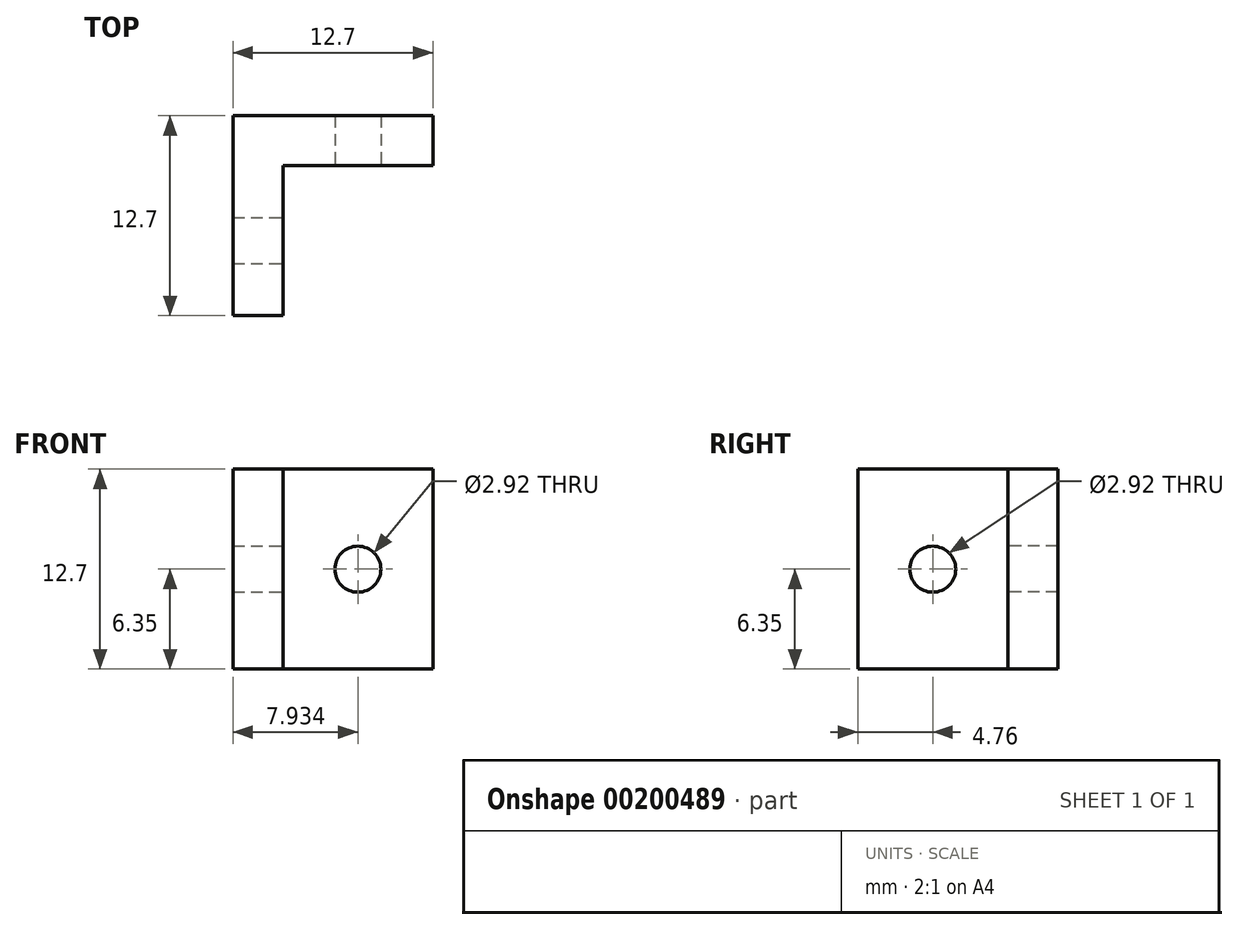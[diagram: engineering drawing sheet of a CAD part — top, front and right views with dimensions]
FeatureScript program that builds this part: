
annotation { "Feature Type Name" : "Feature", "Feature Type Description" : "" }
export const myFeature = defineFeature(function(context is Context, id is Id, definition is map)
    precondition{}
    {
        {
            var Q0;
            Q0=qCreatedBy(makeId("Top.planeOp"),FACE);
            var sketch = newSketch(context, id + "F0", { "sketchPlane" : qUnion([Q0])});
            skLineSegment(sketch, "E0", {"start": v(-46.71, 19.35) * mm, "end": v(-46.71, 32.05) * mm});
            skLineSegment(sketch, "E1", {"start": v(-46.71, 32.05) * mm, "end": v(-34.01, 32.05) * mm});
            skLineSegment(sketch, "E2", {"start": v(-46.71, 19.35) * mm, "end": v(-43.54, 19.35) * mm});
            skLineSegment(sketch, "E3", {"start": v(-43.54, 19.35) * mm, "end": v(-43.54, 32.05) * mm});
            skLineSegment(sketch, "E4", {"start": v(-43.54, 32.05) * mm, "end": v(-43.54, 28.87) * mm});
            skLineSegment(sketch, "E5", {"start": v(-43.54, 28.87) * mm, "end": v(-34.01, 28.87) * mm});
            skLineSegment(sketch, "E6", {"start": v(-34.01, 28.87) * mm, "end": v(-34.01, 32.05) * mm});
            skSolve(sketch);
        }
        {
            var Q0;
            Q0 = qSketchRegion(id + "F0", true);
            extrude(context, id + "F1", {"entities" : qUnion([Q0]), "depth" : 12.7 * mm});
        }
        {
            var Q0;
            Q0=makeQuery(id+"F1.opExtrude","SWEPT_FACE",FACE,{"disambiguationData":[OSD([sQuery(id+"F0.wireOp",EDGE,"E5")])]});
            var sketch = newSketch(context, id + "F2", { "sketchPlane" : qUnion([Q0])});
            skCircle(sketch, "E7", {"center": v(-38.78, 6.35) * mm, "radius": 1.46 * mm});
            skSolve(sketch);
        }
        {
            var Q0;
            Q0=makeQuery(id+"F1.opExtrude","SWEPT_FACE",FACE,{"disambiguationData":[OSD([sQuery(id+"F0.wireOp",EDGE,"E3")])]});
            var sketch = newSketch(context, id + "F3", { "sketchPlane" : qUnion([Q0])});
            skCircle(sketch, "E8", {"center": v(24.11, 6.35) * mm, "radius": 1.46 * mm});
            skSolve(sketch);
        }
        {
            var Q0;
            Q0 = qSketchRegion(id + "F2", true);
            extrude(context, id + "F4", {"entities" : qUnion([Q0]), "operationType" : NewBodyOperationType.REMOVE, "oppositeDirection" : true, "depth" : 25.4 * mm});
        }
        {
            var Q0;
            Q0 = qSketchRegion(id + "F3", true);
            extrude(context, id + "F5", {"entities" : qUnion([Q0]), "operationType" : NewBodyOperationType.REMOVE, "oppositeDirection" : true, "depth" : 25.4 * mm});
        }
    });
